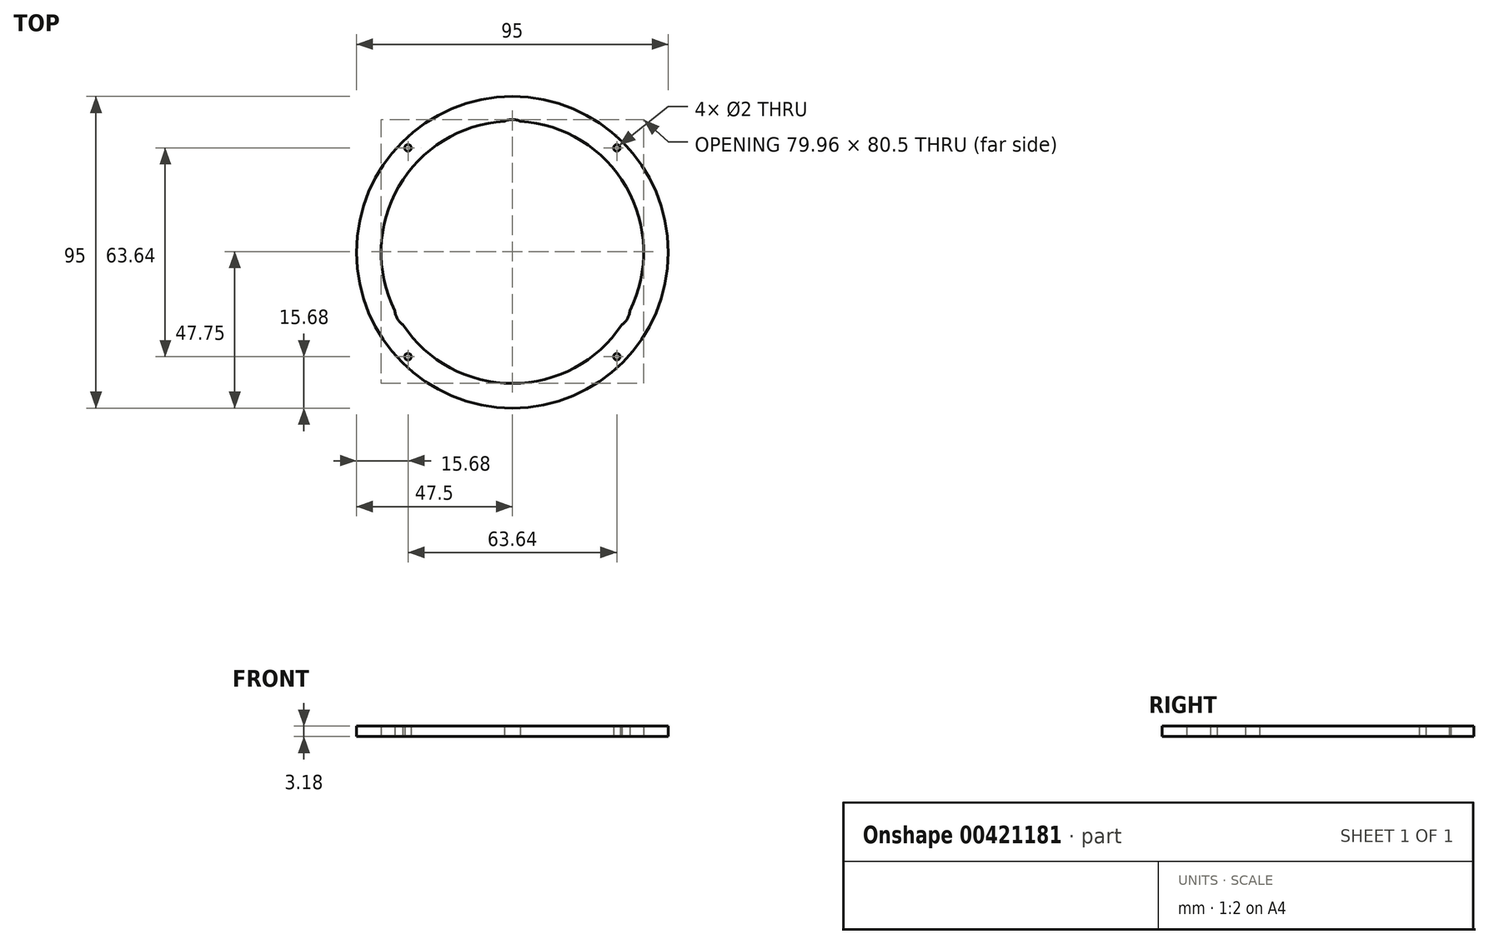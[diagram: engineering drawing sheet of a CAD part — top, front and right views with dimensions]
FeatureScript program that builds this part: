
annotation { "Feature Type Name" : "Feature", "Feature Type Description" : "" }
export const myFeature = defineFeature(function(context is Context, id is Id, definition is map)
    precondition{}
    {
        {
            var Q0;
            Q0=qCreatedBy(makeId("Top.planeOp"),FACE);
            var sketch = newSketch(context, id + "F0", { "sketchPlane" : qUnion([Q0])});
            skCircle(sketch, "E0", {"center": v(0, 0) * mm, "radius": 47.5 * mm});
            skLineSegment(sketch, "E1", {"start": v(0, 0) * mm, "end": v(-35, 0) * mm});
            skCircle(sketch, "E2", {"center": v(-35, 0) * mm, "radius": 2.38 * mm});
            skCircle(sketch, "E3", {"center": v(0, 0) * mm, "radius": 40 * mm});
            skLineSegment(sketch, "E4", {"start": v(0, 0) * mm, "end": v(-31.82, -31.82) * mm});
            skCircle(sketch, "E5", {"center": v(-31.82, -31.82) * mm, "radius": 1 * mm});
            skCircle(sketch, "E6.1.0", {"center": v(31.82, -31.82) * mm, "radius": 1 * mm});
            skCircle(sketch, "E6.2.0", {"center": v(31.82, 31.82) * mm, "radius": 1 * mm});
            skCircle(sketch, "E6.3.0", {"center": v(-31.82, 31.82) * mm, "radius": 1 * mm});
            skCircle(sketch, "E7.MirrorC", {"center": v(35, 0) * mm, "radius": 2.38 * mm});
            skLineSegment(sketch, "E8", {"start": v(0, 0) * mm, "end": v(0, 35) * mm});
            skCircle(sketch, "E9", {"center": v(0, 35) * mm, "radius": 5.5 * mm});
            skCircle(sketch, "E10.1.0", {"center": v(-30.31, -17.5) * mm, "radius": 5.5 * mm});
            skCircle(sketch, "E10.2.0", {"center": v(30.31, -17.5) * mm, "radius": 5.5 * mm});
            skSolve(sketch);
        }
        {
            var Q0;
            Q0 = qSketchRegion(id + "F0", true);
            extrude(context, id + "F1", {"entities" : qUnion([Q0]), "depth" : 3.17 * mm});
        }
    });
